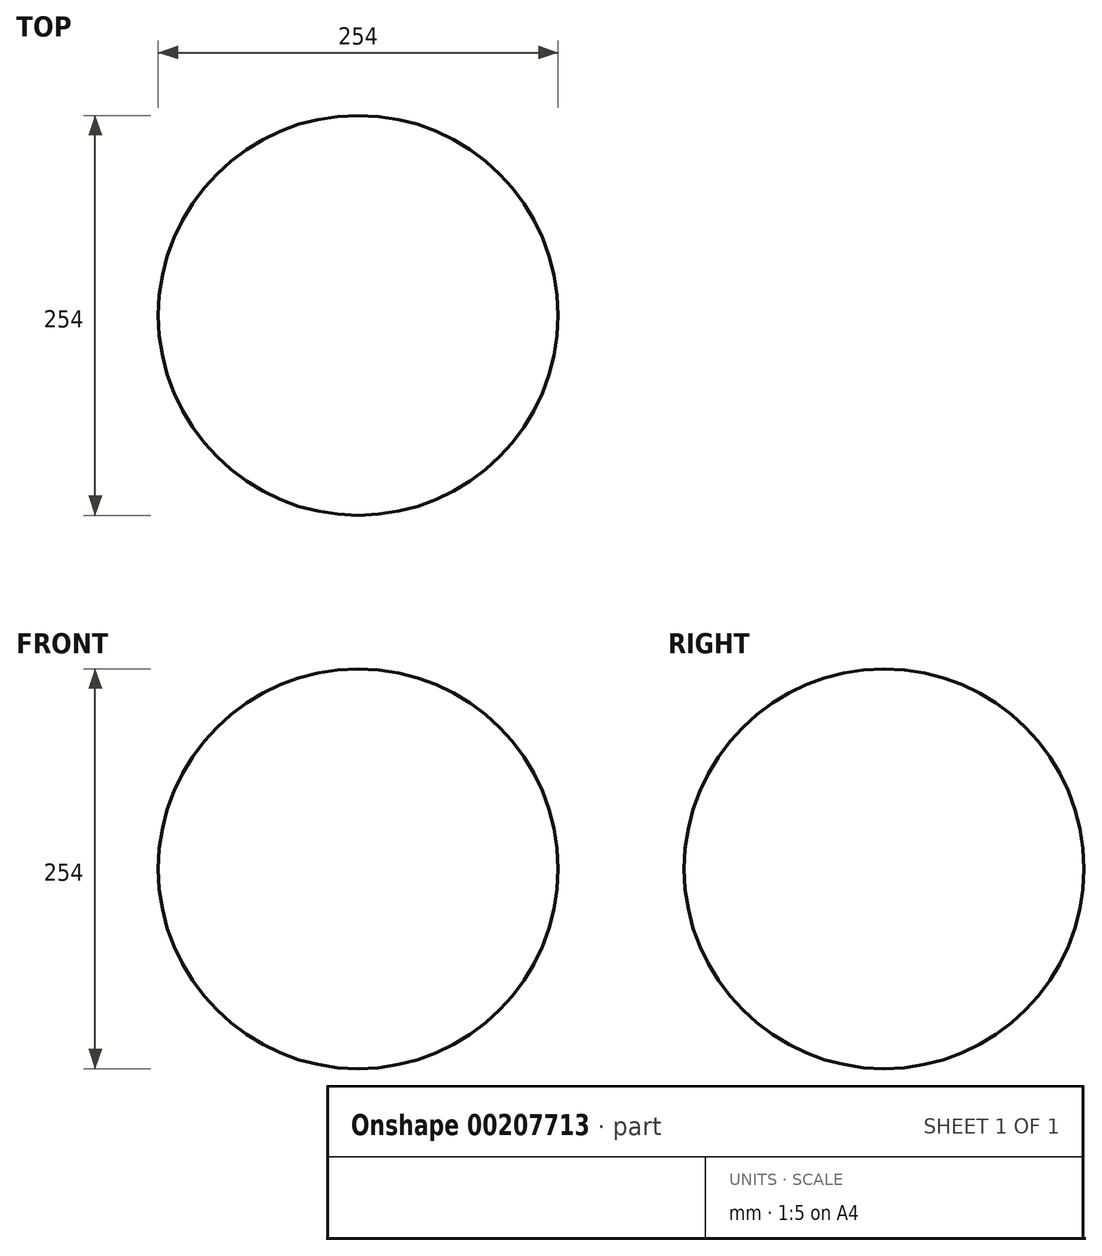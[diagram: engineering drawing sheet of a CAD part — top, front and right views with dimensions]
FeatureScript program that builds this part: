
annotation { "Feature Type Name" : "Feature", "Feature Type Description" : "" }
export const myFeature = defineFeature(function(context is Context, id is Id, definition is map)
    precondition{}
    {
        {
            var Q0;
            Q0=qCreatedBy(makeId("Front.planeOp"),FACE);
            var sketch = newSketch(context, id + "F0", { "sketchPlane" : qUnion([Q0])});
            skArc(sketch, "E0", {"start": v(-127, 0) * mm, "mid": v(0, -127) * mm, "end": v(127, 0) * mm});
            skLineSegment(sketch, "E1", {"start": v(-127, 0) * mm, "end": v(127, 0) * mm});
            skSolve(sketch);
        }
        {
            var Q0;
            Q0 = qSketchRegion(id + "F0", true);
            var Q1;
            Q1=sQuery(id+"F0.wireOp",EDGE,"E1");
            revolve(context, id + "F1", {"entities" : qUnion([Q0]), "axis" : qUnion([Q1]), "revolveType" : RevolveType.FULL});
        }
    });
